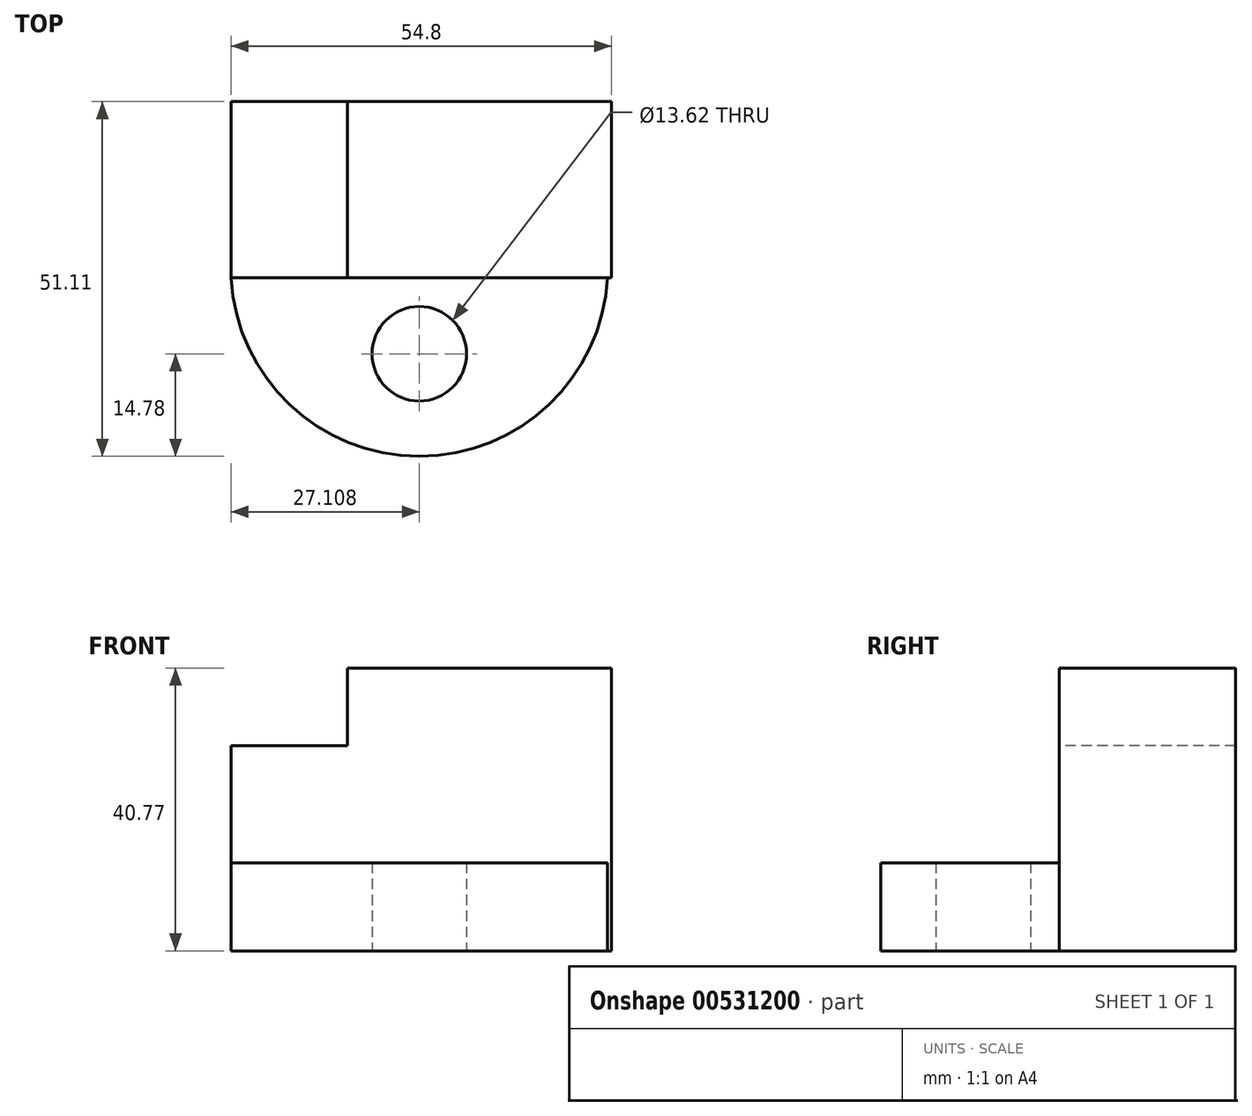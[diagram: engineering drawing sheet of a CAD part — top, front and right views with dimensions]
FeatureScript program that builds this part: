
annotation { "Feature Type Name" : "Feature", "Feature Type Description" : "" }
export const myFeature = defineFeature(function(context is Context, id is Id, definition is map)
    precondition{}
    {
        {
            var Q0;
            Q0=qCreatedBy(makeId("Top.planeOp"),FACE);
            var sketch = newSketch(context, id + "F0", { "sketchPlane" : qUnion([Q0])});
            skArc(sketch, "E0", {"start": v(-29.44, 0) * mm, "mid": v(-2.33, -25.71) * mm, "end": v(24.78, 0) * mm});
            skLineSegment(sketch, "E1", {"start": v(-29.44, 0) * mm, "end": v(24.78, 0) * mm});
            skCircle(sketch, "E2", {"center": v(-2.33, -10.93) * mm, "radius": 6.81 * mm});
            skSolve(sketch);
        }
        {
            var Q0;
            Q0 = qSketchRegion(id + "F0", true);
            extrude(context, id + "F1", {"entities" : qUnion([Q0]), "depth" : 12.7 * mm, "offsetDistance" : 25.4 * mm});
        }
        {
            var Q0;
            Q0=qCreatedBy(makeId("Front.planeOp"),FACE);
            var sketch = newSketch(context, id + "F2", { "sketchPlane" : qUnion([Q0])});
            skLineSegment(sketch, "E3.bottom", {"start": v(25.36, 0) * mm, "end": v(-29.44, 0) * mm});
            skLineSegment(sketch, "E3.top", {"start": v(25.36, 40.77) * mm, "end": v(-29.44, 40.77) * mm});
            skLineSegment(sketch, "E3.left", {"start": v(25.36, 0) * mm, "end": v(25.36, 40.77) * mm});
            skLineSegment(sketch, "E3.right", {"start": v(-29.44, 0) * mm, "end": v(-29.44, 40.77) * mm});
            skSolve(sketch);
        }
        {
            var Q0;
            Q0 = qSketchRegion(id + "F2", true);
            extrude(context, id + "F3", {"entities" : qUnion([Q0]), "oppositeDirection" : true, "depth" : 25.4 * mm, "offsetDistance" : 25.4 * mm});
        }
        {
            var Q0;
            Q0=makeQuery(id+"F3.opExtrude","CAP_FACE",FACE,{"disambiguationData":[OSD([sQuery(id+"F2.wireOp",EDGE,"E3.bottom"),sQuery(id+"F2.wireOp",EDGE,"E3.top"),sQuery(id+"F2.wireOp",EDGE,"E3.left"),sQuery(id+"F2.wireOp",EDGE,"E3.right")])],"isStart":true});
            var sketch = newSketch(context, id + "F4", { "sketchPlane" : qUnion([Q0])});
            skLineSegment(sketch, "E4.bottom", {"start": v(-29.44, 40.77) * mm, "end": v(-12.66, 40.77) * mm});
            skLineSegment(sketch, "E4.top", {"start": v(-29.44, 29.58) * mm, "end": v(-12.66, 29.58) * mm});
            skLineSegment(sketch, "E4.left", {"start": v(-29.44, 40.77) * mm, "end": v(-29.44, 29.58) * mm});
            skLineSegment(sketch, "E4.right", {"start": v(-12.66, 40.77) * mm, "end": v(-12.66, 29.58) * mm});
            skSolve(sketch);
        }
        {
            var Q0;
            Q0=makeQuery(id+"F4.imprint","IMPRINT",FACE,{"disambiguationData":[TD([[makeQuery(id+"F4.imprint","IMPRINT",EDGE,{"derivedFrom":sQuery(id+"F4.wireOp",EDGE,"E4.bottom")}),1.0]])]});
            extrude(context, id + "F5", {"entities" : qUnion([Q0]), "operationType" : NewBodyOperationType.REMOVE, "endBound" : BoundingType.THROUGH_ALL, "oppositeDirection" : true, "depth" : 25.4 * mm, "offsetDistance" : 25.4 * mm});
        }
    });
